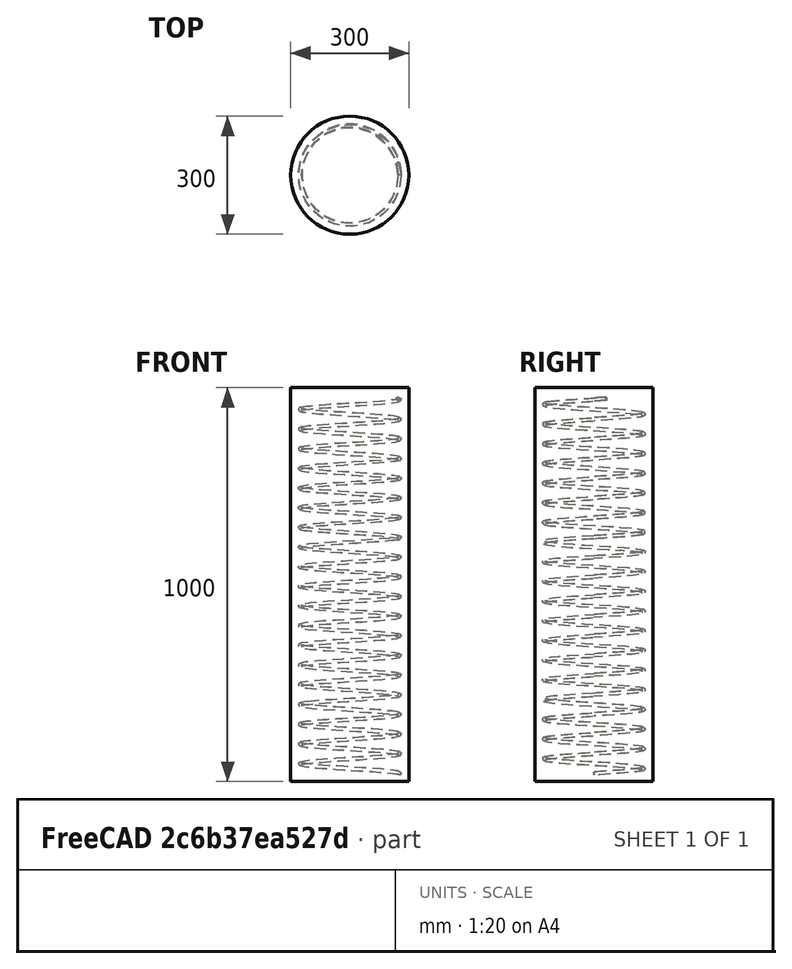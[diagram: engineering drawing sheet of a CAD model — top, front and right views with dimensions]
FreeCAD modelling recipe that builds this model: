
FCSTD DOCUMENT  (FreeCAD 0.19R20802 (Git))
Label: helical_rebar_drawing_dimension
License: All rights reserved
LicenseURL: http://en.wikipedia.org/wiki/All_rights_reserved
objects: TechDraw::DrawViewSymbolPython×12, TechDraw::DrawSVGTemplate×6, TechDraw::DrawPage×6, Part::FeaturePython×2, Part::Part2DObjectPython×1, Part::Helix×1
note: 4 computed .brp shape members not serialized (recipe doc carries the construction recipe); baked Part::Feature solids carry a one-line shape summary decoded from their .brp

FEATURE [Part::Part2DObjectPython] Circle  # Draft 2D object (typed FeaturePython)
  Area = 0
  FirstAngle = 0
  LastAngle = 0
  MakeFace = false
  Radius = 150
FEATURE [Part::FeaturePython] Structure  # Arch/BIM 172 (typed FeaturePython)
  Base = -> Circle
  FaceMaker = 0
  Height = 1000
  HorizontalArea = 70685.8
  IfcData = attributes={"GlobalId": {"name": "GlobalId", "type": "IfcGloballyUniqueId", "is_enum": false, "enum_values": []}, "Description": {"... (+484 chars omitted),+1 more (map truncated)
  IfcType = 172
  Length = 0
  MoveBase = false
  MoveWithHost = false
  Nodes = (2) [(0,-1.22074e-14,0),(0,-1.22074e-14,1000)]
  NodesOffset = 0
  Normal = (0,0,0)
  PerimeterLength = 942.478
  PredefinedType = 0
  VerticalArea = 942478
  Width = 700
FEATURE [Part::Helix] Helix
  Angle = 0
  AttacherType = Attacher::AttachEngine3D
  Height = 952
  LocalCoord = 0
  Pitch = 50
  Placement = pos=(0,-1.22e-14,24) rot=(0,0,1;0rad)
  Radius = 126
  Style = 0
  Support = -> [Structure]
FEATURE [Part::FeaturePython] Rebar  label="HelicalRebar"  # Arch/BIM 110 (typed FeaturePython)
  Amount = 1
  Base = -> Helix
  BottomCover = 20
  Diameter = 8
  Direction = (0,0,0)
  Distance = 0
  HorizontalArea = 0
  Host = -> Structure
  IfcType = 110
  Length = 0
  Mark = HR
  MoveBase = false
  MoveWithHost = false
  OffsetEnd = 4
  OffsetStart = 4
  PerimeterLength = 0
  Pitch = 50
  PlacementList = 1 placements: [(0,0,-4)]
  RebarShape = 5
  Rounding = 0
  SideCover = 20
  Spacing = 0
  TopCover = 20
  TotalLength = 0
  VerticalArea = 0
FEATURE [TechDraw::DrawSVGTemplate] Template
  Height = 210
  Orientation = 1
  Width = 297
FEATURE [TechDraw::DrawViewSymbolPython] ReinforcementDrawingView  label="Front View"  # drawing view (typed FeaturePython)
  DimensionBottomOffset = 10
  DimensionLeftOffset = 10
  DimensionRightOffset = 16
  DimensionTopOffset = 10
  Height = 1000
  LeftOffset = 123
  LockPosition = false
  MaxHeight = 210
  MaxWidth = 297
  MinBottomOffset = 20
  MinRightOffset = 20
  PositionType = 0
  Rebars = -> [Rebar]
  RebarsColorStyle = 0
  RebarsStrokeWidth = 0.35
  Rotation = 0
  Scale = 0.17
  ScaleType = 1
  Structure = -> Structure
  StructureColorStyle = 0
  StructureStrokeWidth = 0.5
  Symbol = <blob: 29253 chars omitted>
  Template = -> Template
  TopOffset = 20
  View = 0
  VisibleRebars = -> [Rebar]
  Width = 300
  X = 148.5
  Y = 105
  expr: TopOffset = .Template.Height.Value / 2 - .Height.Value * .Scale / 2
  expr: LeftOffset = .Template.Width.Value / 2 - .Width.Value * .Scale / 2
FEATURE [TechDraw::DrawViewSymbolPython] ReinforcementDimensioning  # drawing view (typed FeaturePython)
  DimensionBottomOffset = 10
  DimensionFormat = %M %C⌀%D,span=%S
  DimensionLeftOffset = 10
  DimensionRightOffset = 10
  DimensionTopOffset = 10
  Font = DejaVu Sans
  FontSize = 3
  LineEndSymbol = 0
  LineMidPointSymbol = 1
  LineStartSymbol = 3
  LineStyle = 0
  LockPosition = false
  MultiRebar_LineEndSymbol = 0
  MultiRebar_LineStartSymbol = 0
  MultiRebar_OuterDimension = true
  MultiRebar_TextPositionType = 0
  ParentDrawingView = -> ReinforcementDrawingView
  Rebar = -> Rebar
  Rotation = 0
  Scale = 0.17
  ScaleType = 2
  SingleRebar_LineEndSymbol = 0
  SingleRebar_LineStartSymbol = 3
  SingleRebar_OuterDimension = false
  SingleRebar_TextPositionType = 1
  StrokeWidth = 0.25
  Symbol = <blob: 4596 chars omitted>
  TextPositionType = 0
  WayPoints = (2) [(0,0,0),(50,0,0)]
  WayPointsType = 0
  X = 148.5
  Y = 105
FEATURE [TechDraw::DrawPage] TechDraw__DrawPage  label="Structure Drawing"
  KeepUpdated = true
  NextBalloonIndex = 1
  ProjectionType = 0
  Template = -> Template
  Views = -> [ReinforcementDrawingView,ReinforcementDimensioning]
FEATURE [TechDraw::DrawSVGTemplate] Template001
  Height = 210
  Orientation = 1
  Width = 297
FEATURE [TechDraw::DrawViewSymbolPython] ReinforcementDrawingView001  label="Rear View"  # drawing view (typed FeaturePython)
  DimensionBottomOffset = 10
  DimensionLeftOffset = 16
  DimensionRightOffset = 10
  DimensionTopOffset = 10
  Height = 1000
  LeftOffset = 123
  LockPosition = false
  MaxHeight = 210
  MaxWidth = 297
  MinBottomOffset = 20
  MinRightOffset = 20
  PositionType = 0
  Rebars = -> [Rebar]
  RebarsColorStyle = 0
  RebarsStrokeWidth = 0.35
  Rotation = 0
  Scale = 0.17
  ScaleType = 1
  Structure = -> Structure
  StructureColorStyle = 0
  StructureStrokeWidth = 0.5
  Symbol = <blob: 29302 chars omitted>
  Template = -> Template001
  TopOffset = 20
  View = 1
  VisibleRebars = -> [Rebar]
  Width = 300
  X = 148.5
  Y = 105
  expr: TopOffset = .Template.Height.Value / 2 - .Height.Value * .Scale / 2
  expr: LeftOffset = .Template.Width.Value / 2 - .Width.Value * .Scale / 2
FEATURE [TechDraw::DrawViewSymbolPython] ReinforcementDimensioning001  # drawing view (typed FeaturePython)
  DimensionBottomOffset = 10
  DimensionFormat = %M %C⌀%D,span=%S
  DimensionLeftOffset = 10
  DimensionRightOffset = 10
  DimensionTopOffset = 10
  Font = DejaVu Sans
  FontSize = 3
  LineEndSymbol = 0
  LineMidPointSymbol = 1
  LineStartSymbol = 3
  LineStyle = 0
  LockPosition = false
  MultiRebar_LineEndSymbol = 0
  MultiRebar_LineStartSymbol = 0
  MultiRebar_OuterDimension = true
  MultiRebar_TextPositionType = 0
  ParentDrawingView = -> ReinforcementDrawingView001
  Rebar = -> Rebar
  Rotation = 0
  Scale = 0.17
  ScaleType = 2
  SingleRebar_LineEndSymbol = 0
  SingleRebar_LineStartSymbol = 3
  SingleRebar_OuterDimension = false
  SingleRebar_TextPositionType = 1
  StrokeWidth = 0.25
  Symbol = <blob: 4644 chars omitted>
  TextPositionType = 0
  WayPoints = (2) [(0,0,0),(50,0,0)]
  WayPointsType = 0
  X = 148.5
  Y = 105
FEATURE [TechDraw::DrawPage] TechDraw__DrawPage001  label="Structure Drawing001"
  KeepUpdated = true
  NextBalloonIndex = 1
  ProjectionType = 0
  Template = -> Template001
  Views = -> [ReinforcementDrawingView001,ReinforcementDimensioning001]
FEATURE [TechDraw::DrawSVGTemplate] Template002
  Height = 210
  Orientation = 1
  Width = 297
FEATURE [TechDraw::DrawViewSymbolPython] ReinforcementDrawingView002  label="Left View"  # drawing view (typed FeaturePython)
  DimensionBottomOffset = 10
  DimensionLeftOffset = 16
  DimensionRightOffset = 10
  DimensionTopOffset = 10
  Height = 1000
  LeftOffset = 123.17
  LockPosition = false
  MaxHeight = 210
  MaxWidth = 297
  MinBottomOffset = 20
  MinRightOffset = 20
  PositionType = 0
  Rebars = -> [Rebar]
  RebarsColorStyle = 0
  RebarsStrokeWidth = 0.35
  Rotation = 0
  Scale = 0.17
  ScaleType = 1
  Structure = -> Structure
  StructureColorStyle = 0
  StructureStrokeWidth = 0.5
  Symbol = <blob: 29419 chars omitted>
  Template = -> Template002
  TopOffset = 20
  View = 2
  VisibleRebars = -> [Rebar]
  Width = 298
  X = 148.5
  Y = 105
  expr: TopOffset = .Template.Height.Value / 2 - .Height.Value * .Scale / 2
  expr: LeftOffset = .Template.Width.Value / 2 - .Width.Value * .Scale / 2
FEATURE [TechDraw::DrawViewSymbolPython] ReinforcementDimensioning002  # drawing view (typed FeaturePython)
  DimensionBottomOffset = 10
  DimensionFormat = %M %C⌀%D,span=%S
  DimensionLeftOffset = 10
  DimensionRightOffset = 10
  DimensionTopOffset = 10
  Font = DejaVu Sans
  FontSize = 3
  LineEndSymbol = 0
  LineMidPointSymbol = 1
  LineStartSymbol = 3
  LineStyle = 0
  LockPosition = false
  MultiRebar_LineEndSymbol = 0
  MultiRebar_LineStartSymbol = 0
  MultiRebar_OuterDimension = true
  MultiRebar_TextPositionType = 0
  ParentDrawingView = -> ReinforcementDrawingView002
  Rebar = -> Rebar
  Rotation = 0
  Scale = 0.17
  ScaleType = 2
  SingleRebar_LineEndSymbol = 0
  SingleRebar_LineStartSymbol = 3
  SingleRebar_OuterDimension = false
  SingleRebar_TextPositionType = 1
  StrokeWidth = 0.25
  Symbol = <blob: 4656 chars omitted>
  TextPositionType = 0
  WayPoints = (2) [(0,0,0),(50,0,0)]
  WayPointsType = 0
  X = 148.5
  Y = 105
FEATURE [TechDraw::DrawPage] TechDraw__DrawPage002  label="Structure Drawing002"
  KeepUpdated = true
  NextBalloonIndex = 1
  ProjectionType = 0
  Template = -> Template002
  Views = -> [ReinforcementDrawingView002,ReinforcementDimensioning002]
FEATURE [TechDraw::DrawSVGTemplate] Template003
  Height = 210
  Orientation = 1
  Width = 297
FEATURE [TechDraw::DrawViewSymbolPython] ReinforcementDrawingView003  label="Right View"  # drawing view (typed FeaturePython)
  DimensionBottomOffset = 10
  DimensionLeftOffset = 10
  DimensionRightOffset = 16
  DimensionTopOffset = 10
  Height = 1000
  LeftOffset = 123.17
  LockPosition = false
  MaxHeight = 210
  MaxWidth = 297
  MinBottomOffset = 20
  MinRightOffset = 20
  PositionType = 0
  Rebars = -> [Rebar]
  RebarsColorStyle = 0
  RebarsStrokeWidth = 0.35
  Rotation = 0
  Scale = 0.17
  ScaleType = 1
  Structure = -> Structure
  StructureColorStyle = 0
  StructureStrokeWidth = 0.5
  Symbol = <blob: 29417 chars omitted>
  Template = -> Template003
  TopOffset = 20
  View = 3
  VisibleRebars = -> [Rebar]
  Width = 298
  X = 148.5
  Y = 105
  expr: TopOffset = .Template.Height.Value / 2 - .Height.Value * .Scale / 2
  expr: LeftOffset = .Template.Width.Value / 2 - .Width.Value * .Scale / 2
FEATURE [TechDraw::DrawViewSymbolPython] ReinforcementDimensioning003  # drawing view (typed FeaturePython)
  DimensionBottomOffset = 10
  DimensionFormat = %M %C⌀%D,span=%S
  DimensionLeftOffset = 10
  DimensionRightOffset = 10
  DimensionTopOffset = 10
  Font = DejaVu Sans
  FontSize = 3
  LineEndSymbol = 0
  LineMidPointSymbol = 1
  LineStartSymbol = 3
  LineStyle = 0
  LockPosition = false
  MultiRebar_LineEndSymbol = 0
  MultiRebar_LineStartSymbol = 0
  MultiRebar_OuterDimension = true
  MultiRebar_TextPositionType = 0
  ParentDrawingView = -> ReinforcementDrawingView003
  Rebar = -> Rebar
  Rotation = 0
  Scale = 0.17
  ScaleType = 2
  SingleRebar_LineEndSymbol = 0
  SingleRebar_LineStartSymbol = 3
  SingleRebar_OuterDimension = false
  SingleRebar_TextPositionType = 1
  StrokeWidth = 0.25
  Symbol = <blob: 4609 chars omitted>
  TextPositionType = 0
  WayPoints = (2) [(0,0,0),(50,0,0)]
  WayPointsType = 0
  X = 148.5
  Y = 105
FEATURE [TechDraw::DrawPage] TechDraw__DrawPage003  label="Structure Drawing003"
  KeepUpdated = true
  NextBalloonIndex = 1
  ProjectionType = 0
  Template = -> Template003
  Views = -> [ReinforcementDrawingView003,ReinforcementDimensioning003]
FEATURE [TechDraw::DrawSVGTemplate] Template004
  Height = 210
  Orientation = 1
  Width = 297
FEATURE [TechDraw::DrawViewSymbolPython] ReinforcementDrawingView004  label="Top View"  # drawing view (typed FeaturePython)
  DimensionBottomOffset = 10
  DimensionLeftOffset = 10
  DimensionRightOffset = 16
  DimensionTopOffset = 10
  Height = 298
  LeftOffset = 62.9295
  LockPosition = false
  MaxHeight = 210
  MaxWidth = 297
  MinBottomOffset = 20
  MinRightOffset = 20
  PositionType = 0
  Rebars = -> [Rebar]
  RebarsColorStyle = 0
  RebarsStrokeWidth = 0.35
  Rotation = 0
  Scale = 0.57047
  ScaleType = 1
  Structure = -> Structure
  StructureColorStyle = 0
  StructureStrokeWidth = 0.5
  Symbol = <blob: 19191 chars omitted>
  Template = -> Template004
  TopOffset = 20
  View = 4
  VisibleRebars = -> [Rebar]
  Width = 300
  X = 148.5
  Y = 105
  expr: TopOffset = .Template.Height.Value / 2 - .Height.Value * .Scale / 2
  expr: LeftOffset = .Template.Width.Value / 2 - .Width.Value * .Scale / 2
FEATURE [TechDraw::DrawViewSymbolPython] ReinforcementDimensioning004  # drawing view (typed FeaturePython)
  DimensionBottomOffset = 10
  DimensionFormat = %M %C⌀%D,span=%S
  DimensionLeftOffset = 10
  DimensionRightOffset = 10
  DimensionTopOffset = 10
  Font = DejaVu Sans
  FontSize = 3
  LineEndSymbol = 0
  LineMidPointSymbol = 1
  LineStartSymbol = 3
  LineStyle = 0
  LockPosition = false
  MultiRebar_LineEndSymbol = 0
  MultiRebar_LineStartSymbol = 0
  MultiRebar_OuterDimension = true
  MultiRebar_TextPositionType = 0
  ParentDrawingView = -> ReinforcementDrawingView004
  Rebar = -> Rebar
  Rotation = 0
  Scale = 0.57047
  ScaleType = 2
  SingleRebar_LineEndSymbol = 0
  SingleRebar_LineStartSymbol = 3
  SingleRebar_OuterDimension = false
  SingleRebar_TextPositionType = 1
  StrokeWidth = 0.25
  Symbol = <svg version="1.1" xmlns="http://www.w3.org/2000/svg" xmlns:xlink="http://www.w3.org/1999/xlink" xmlns:freecad="http://www.freecadweb.org/wiki/index.php?title=Svg_Namespace" width="300.0mm" height="298.0mm" viewBox="0 0 300.0 298.0"><g transform="translate(150.0, 148.9063311147081)"><g><path d="M167.52941176470588 -2.28e-13 L126.0 -2.28e-13" style="stroke:#00007f;stroke-width:0.4382352941176471;stroke-linecap:round;fill:none;" stroke-dasharray="" /><g id="line_mid_points" /><path d="M0,0 -8,-1.5 V1.5 L0,0" style="stroke:#00007f;fill:#00007f;stroke-width:0.4382352941176471;stroke-linecap:round;stroke-linejoin:bevel;" transform="translate(126.0 -2.28e-13) rotate(180.0 0 0)" /></g><text x="167.52941176470588" y="2.629411764705655" style="white-space:pre;" fill="#005400" font-family="DejaVu Sans" font-size="5.258823529411766" text-anchor="start" dominant-baseline="baseline" xml:space="preserve">HR 1⌀8,span=953</text></g></svg>
  TextPositionType = 0
  WayPoints = (2) [(0,0,0),(50,0,0)]
  WayPointsType = 0
  X = 148.5
  Y = 105
FEATURE [TechDraw::DrawPage] TechDraw__DrawPage004  label="Structure Drawing004"
  KeepUpdated = true
  NextBalloonIndex = 1
  ProjectionType = 0
  Template = -> Template004
  Views = -> [ReinforcementDrawingView004,ReinforcementDimensioning004]
FEATURE [TechDraw::DrawSVGTemplate] Template005
  Height = 210
  Orientation = 1
  Width = 297
FEATURE [TechDraw::DrawViewSymbolPython] ReinforcementDrawingView005  label="Bottom View"  # drawing view (typed FeaturePython)
  DimensionBottomOffset = 10
  DimensionLeftOffset = 10
  DimensionRightOffset = 16
  DimensionTopOffset = 10
  Height = 298
  LeftOffset = 62.9295
  LockPosition = false
  MaxHeight = 210
  MaxWidth = 297
  MinBottomOffset = 20
  MinRightOffset = 20
  PositionType = 0
  Rebars = -> [Rebar]
  RebarsColorStyle = 0
  RebarsStrokeWidth = 0.35
  Rotation = 0
  Scale = 0.57047
  ScaleType = 1
  Structure = -> Structure
  StructureColorStyle = 0
  StructureStrokeWidth = 0.5
  Symbol = <blob: 19189 chars omitted>
  Template = -> Template005
  TopOffset = 20
  View = 5
  VisibleRebars = -> [Rebar]
  Width = 300
  X = 148.5
  Y = 105
  expr: TopOffset = .Template.Height.Value / 2 - .Height.Value * .Scale / 2
  expr: LeftOffset = .Template.Width.Value / 2 - .Width.Value * .Scale / 2
FEATURE [TechDraw::DrawViewSymbolPython] ReinforcementDimensioning005  # drawing view (typed FeaturePython)
  DimensionBottomOffset = 10
  DimensionFormat = %M %C⌀%D,span=%S
  DimensionLeftOffset = 10
  DimensionRightOffset = 10
  DimensionTopOffset = 10
  Font = DejaVu Sans
  FontSize = 3
  LineEndSymbol = 0
  LineMidPointSymbol = 1
  LineStartSymbol = 3
  LineStyle = 0
  LockPosition = false
  MultiRebar_LineEndSymbol = 0
  MultiRebar_LineStartSymbol = 0
  MultiRebar_OuterDimension = true
  MultiRebar_TextPositionType = 0
  ParentDrawingView = -> ReinforcementDrawingView005
  Rebar = -> Rebar
  Rotation = 0
  Scale = 0.57047
  ScaleType = 2
  SingleRebar_LineEndSymbol = 0
  SingleRebar_LineStartSymbol = 3
  SingleRebar_OuterDimension = false
  SingleRebar_TextPositionType = 1
  StrokeWidth = 0.25
  Symbol = <svg version="1.1" xmlns="http://www.w3.org/2000/svg" xmlns:xlink="http://www.w3.org/1999/xlink" xmlns:freecad="http://www.freecadweb.org/wiki/index.php?title=Svg_Namespace" width="300.0mm" height="298.0mm" viewBox="0 0 300.0 298.0"><g transform="translate(150.0, 148.90633111470814)"><g><path d="M167.52941176470588 -1.247e-12 L126.0 -1.247e-12" style="stroke:#00007f;stroke-width:0.4382352941176471;stroke-linecap:round;fill:none;" stroke-dasharray="" /><g id="line_mid_points" /><path d="M0,0 -8,-1.5 V1.5 L0,0" style="stroke:#00007f;fill:#00007f;stroke-width:0.4382352941176471;stroke-linecap:round;stroke-linejoin:bevel;" transform="translate(126.0 -1.247e-12) rotate(180.0 0 0)" /></g><text x="167.52941176470588" y="2.629411764704636" style="white-space:pre;" fill="#005400" font-family="DejaVu Sans" font-size="5.258823529411766" text-anchor="start" dominant-baseline="baseline" xml:space="preserve">HR 1⌀8,span=953</text></g></svg>
  TextPositionType = 0
  WayPoints = (2) [(0,0,0),(50,0,0)]
  WayPointsType = 0
  X = 148.5
  Y = 105
FEATURE [TechDraw::DrawPage] TechDraw__DrawPage005  label="Structure Drawing005"
  KeepUpdated = true
  NextBalloonIndex = 1
  ProjectionType = 0
  Template = -> Template005
  Views = -> [ReinforcementDrawingView005,ReinforcementDimensioning005]
